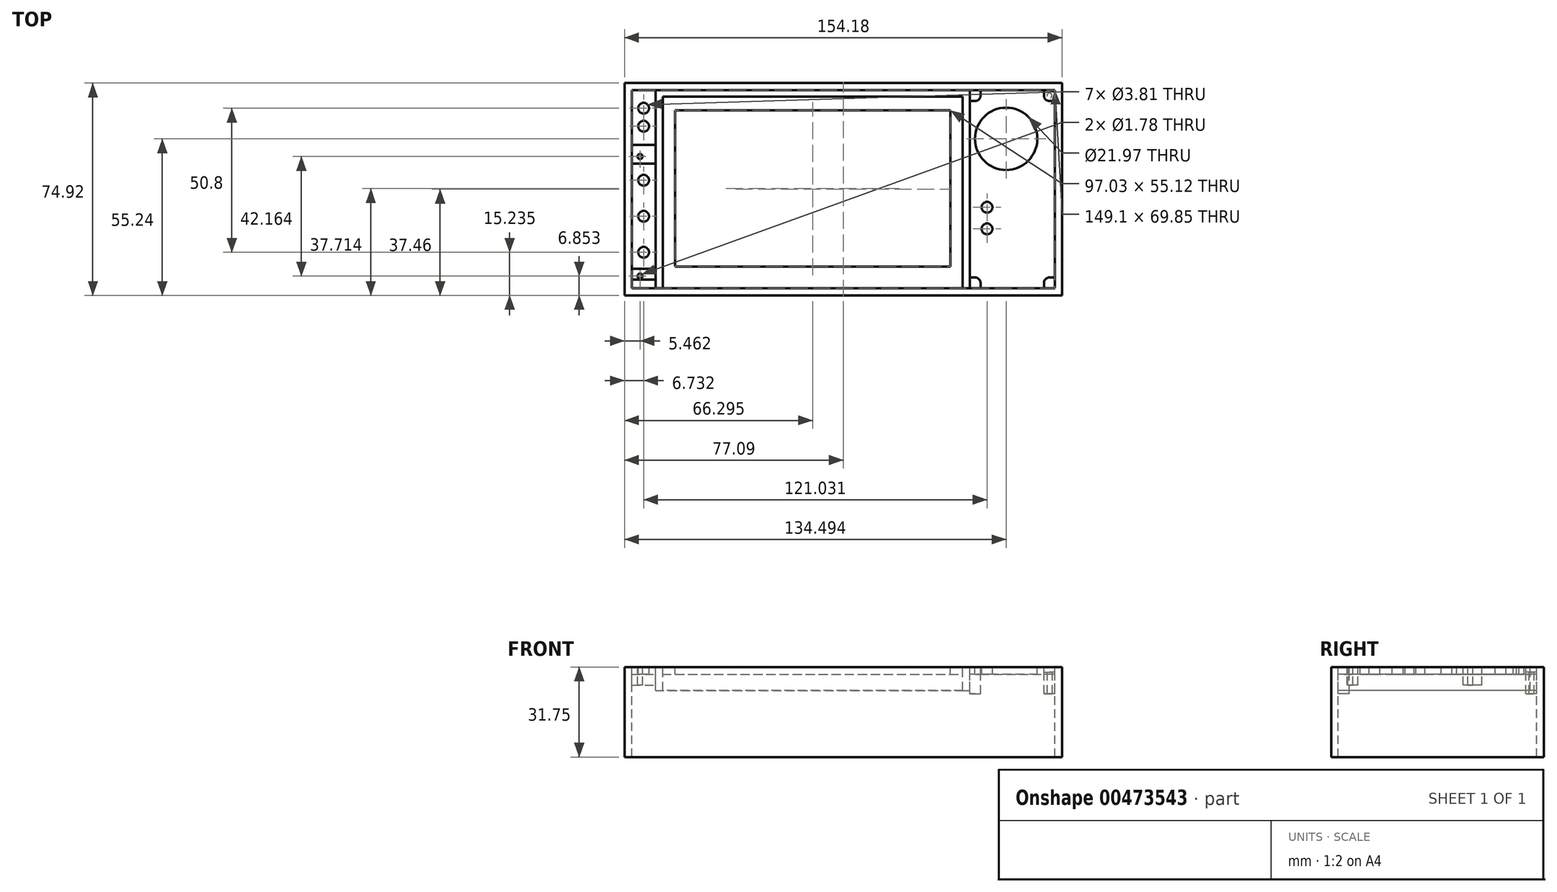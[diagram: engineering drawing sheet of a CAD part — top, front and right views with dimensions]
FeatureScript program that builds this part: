
annotation { "Feature Type Name" : "Feature", "Feature Type Description" : "" }
export const myFeature = defineFeature(function(context is Context, id is Id, definition is map)
    precondition{}
    {
        {
            var Q0;
            Q0=qCreatedBy(makeId("Top.planeOp"),FACE);
            var sketch = newSketch(context, id + "F0", { "sketchPlane" : qUnion([Q0])});
            skLineSegment(sketch, "E0.bottom", {"start": v(77.09, 37.47) * mm, "end": v(-77.09, 37.47) * mm});
            skLineSegment(sketch, "E0.top", {"start": v(77.09, -37.47) * mm, "end": v(-77.09, -37.47) * mm});
            skLineSegment(sketch, "E0.left", {"start": v(77.09, 37.47) * mm, "end": v(77.09, -37.47) * mm});
            skLineSegment(sketch, "E0.right", {"start": v(-77.09, 37.47) * mm, "end": v(-77.09, -37.47) * mm});
            skPoint(sketch, "E0.middle", {"position": v(0, 0) * mm});
            skLineSegment(sketch, "E1.bottom", {"start": v(-59.3, -27.3) * mm, "end": v(37.72, -27.3) * mm});
            skLineSegment(sketch, "E1.top", {"start": v(-59.3, 27.81) * mm, "end": v(37.72, 27.81) * mm});
            skLineSegment(sketch, "E1.left", {"start": v(-59.3, -27.3) * mm, "end": v(-59.3, 27.81) * mm});
            skLineSegment(sketch, "E1.right", {"start": v(37.72, -27.3) * mm, "end": v(37.72, 27.81) * mm});
            skCircle(sketch, "E2", {"center": v(57.4, 17.78) * mm, "radius": 9.53 * mm});
            skLineSegment(sketch, "E3", {"start": v(77.09, -1.9) * mm, "end": v(37.72, 37.47) * mm, "construction": true});
            skLineSegment(sketch, "E4", {"start": v(77.09, 37.47) * mm, "end": v(57.4, 17.78) * mm, "construction": true});
            skCircle(sketch, "E5", {"center": v(57.4, 17.78) * mm, "radius": 13.34 * mm, "construction": true});
            skCircle(sketch, "E6", {"center": v(47.97, 27.2) * mm, "radius": 0.89 * mm});
            skCircle(sketch, "E7", {"center": v(66.83, 8.35) * mm, "radius": 0.89 * mm});
            skCircle(sketch, "E8", {"center": v(57.4, 17.78) * mm, "radius": 10.99 * mm});
            skLineSegment(sketch, "E9.bottom", {"start": v(-74.55, 34.93) * mm, "end": v(74.55, 34.93) * mm});
            skLineSegment(sketch, "E9.top", {"start": v(-74.55, -34.92) * mm, "end": v(74.55, -34.93) * mm});
            skLineSegment(sketch, "E9.left", {"start": v(-63.63, 34.93) * mm, "end": v(-63.63, -34.93) * mm});
            skLineSegment(sketch, "E9.right", {"start": v(42.04, 34.93) * mm, "end": v(42.04, -34.93) * mm});
            skLineSegment(sketch, "E10", {"start": v(-66.17, 34.93) * mm, "end": v(-66.17, -34.93) * mm});
            skLineSegment(sketch, "E11", {"start": v(-74.55, 34.92) * mm, "end": v(-74.55, -34.92) * mm});
            skLineSegment(sketch, "E12", {"start": v(44.58, 34.93) * mm, "end": v(44.58, -34.93) * mm});
            skLineSegment(sketch, "E13", {"start": v(74.55, 34.93) * mm, "end": v(74.55, -34.93) * mm});
            skCircle(sketch, "E14", {"center": v(-70.36, 3.18) * mm, "radius": 1.9 * mm});
            skCircle(sketch, "E15", {"center": v(-70.36, -9.52) * mm, "radius": 1.9 * mm});
            skCircle(sketch, "E16", {"center": v(-70.36, -22.22) * mm, "radius": 1.9 * mm});
            skCircle(sketch, "E17", {"center": v(-70.36, 28.57) * mm, "radius": 1.9 * mm});
            skLineSegment(sketch, "E18", {"start": v(-70.36, 34.92) * mm, "end": v(-70.36, -34.93) * mm, "construction": true});
            skCircle(sketch, "E19", {"center": v(-70.36, 22.22) * mm, "radius": 1.9 * mm});
            skLineSegment(sketch, "E20", {"start": v(42.04, 32.64) * mm, "end": v(-63.63, 32.64) * mm});
            skLineSegment(sketch, "E21", {"start": v(44.58, -34.92) * mm, "end": v(74.55, -4.95) * mm, "construction": true});
            skLineSegment(sketch, "E22", {"start": v(74.55, -34.93) * mm, "end": v(44.58, -4.95) * mm, "construction": true});
            skCircle(sketch, "E23", {"center": v(72.64, 33.02) * mm, "radius": 0.89 * mm});
            skLineSegment(sketch, "E24", {"start": v(44.58, 34.93) * mm, "end": v(59.56, 19.94) * mm, "construction": true});
            skCircle(sketch, "E25", {"center": v(46.48, 33.02) * mm, "radius": 0.89 * mm});
            skCircle(sketch, "E26", {"center": v(46.48, -33.02) * mm, "radius": 0.89 * mm});
            skCircle(sketch, "E27", {"center": v(72.64, -33.02) * mm, "radius": 0.89 * mm});
            skArc(sketch, "E28", {"start": v(48.39, -33.02) * mm, "mid": v(47.83, -31.67) * mm, "end": v(46.48, -31.12) * mm});
            skArc(sketch, "E29", {"start": v(72.64, -31.12) * mm, "mid": v(71.3, -31.67) * mm, "end": v(70.74, -33.02) * mm});
            skArc(sketch, "E30", {"start": v(70.74, 33.02) * mm, "mid": v(71.3, 31.67) * mm, "end": v(72.64, 31.12) * mm});
            skArc(sketch, "E31", {"start": v(46.48, 31.12) * mm, "mid": v(47.83, 31.67) * mm, "end": v(48.39, 33.02) * mm});
            skLineSegment(sketch, "E32", {"start": v(46.48, 31.12) * mm, "end": v(44.58, 31.12) * mm});
            skLineSegment(sketch, "E33", {"start": v(48.39, 34.93) * mm, "end": v(48.39, 33.02) * mm});
            skLineSegment(sketch, "E34", {"start": v(70.74, 34.93) * mm, "end": v(70.74, 33.02) * mm});
            skLineSegment(sketch, "E35", {"start": v(74.55, 31.12) * mm, "end": v(72.64, 31.12) * mm});
            skLineSegment(sketch, "E36", {"start": v(74.55, -31.12) * mm, "end": v(72.64, -31.12) * mm});
            skLineSegment(sketch, "E37", {"start": v(70.74, -33.02) * mm, "end": v(70.74, -34.93) * mm});
            skLineSegment(sketch, "E38", {"start": v(48.39, -33.02) * mm, "end": v(48.39, -34.93) * mm});
            skLineSegment(sketch, "E39", {"start": v(46.48, -31.12) * mm, "end": v(44.58, -31.12) * mm});
            skCircle(sketch, "E40", {"center": v(50.67, -13.97) * mm, "radius": 1.9 * mm});
            skCircle(sketch, "E41", {"center": v(50.67, -6.35) * mm, "radius": 1.9 * mm});
            skLineSegment(sketch, "E42", {"start": v(-66.17, 9.02) * mm, "end": v(-74.55, 9.02) * mm});
            skLineSegment(sketch, "E43", {"start": v(-74.55, 15.62) * mm, "end": v(-66.17, 15.62) * mm});
            skLineSegment(sketch, "E44", {"start": v(-74.55, -28.07) * mm, "end": v(-63.63, -28.07) * mm});
            skLineSegment(sketch, "E45", {"start": v(-66.17, -31.88) * mm, "end": v(-74.55, -31.88) * mm});
            skCircle(sketch, "E46", {"center": v(-71.63, 11.56) * mm, "radius": 0.89 * mm});
            skCircle(sketch, "E47", {"center": v(-71.63, -30.6) * mm, "radius": 0.89 * mm});
            skLineSegment(sketch, "E48", {"start": v(-71.63, 11.56) * mm, "end": v(-70.36, -9.53) * mm, "construction": true});
            skLineSegment(sketch, "E49", {"start": v(-71.63, -30.6) * mm, "end": v(-70.36, -9.52) * mm, "construction": true});
            skSolve(sketch);
        }
        {
            var Q0;
            Q0=makeQuery(id+"F0.imprint","IMPRINT",FACE,{"disambiguationData":[TD([[makeQuery(id+"F0.imprint","IMPRINT",EDGE,{"derivedFrom":sQuery(id+"F0.wireOp",EDGE,"E0.bottom")}),1.0]])]});
            extrude(context, id + "F1", {"entities" : qUnion([Q0]), "oppositeDirection" : true, "depth" : 31.75 * mm, "offsetDistance" : 25.4 * mm});
        }
        {
            var Q0;
            {var subQ6=sQuery(id+"F0.wireOp",EDGE,"E10");Q0=makeQuery(id+"F0.imprint","IMPRINT",FACE,{"disambiguationData":[TD([[makeQuery(id+"F0.imprint","IMPRINT",EDGE,{"derivedFrom":subQ6}),1.0]])]});}
            var Q1;
            {var subQ0=sQuery(id+"F0.wireOp",EDGE,"E9.right");var subQ4=sQuery(id+"F0.wireOp",EDGE,"E9.bottom");var subQ5=makeQuery(id+"F0.imprint","INTERSECT",VERTEX,{"derivedFrom":[subQ4,subQ0]});Q1=makeQuery(id+"F0.imprint","IMPRINT",FACE,{"disambiguationData":[TD([[makeQuery(id+"F0.imprint","IMPRINT",EDGE,{"disambiguationData":[TD([[subQ5,-1.0]])],"derivedFrom":subQ4}),-1.0]])]});}
            var Q2;
            {var subQ5=sQuery(id+"F0.wireOp",EDGE,"E20");Q2=makeQuery(id+"F0.imprint","IMPRINT",FACE,{"disambiguationData":[TD([[makeQuery(id+"F0.imprint","IMPRINT",EDGE,{"derivedFrom":subQ5}),-1.0]])]});}
            var Q3;
            {var subQ4=sQuery(id+"F0.wireOp",EDGE,"E9.left");var subQ5=sQuery(id+"F0.wireOp",EDGE,"E9.top");var subQ6=makeQuery(id+"F0.imprint","INTERSECT",VERTEX,{"derivedFrom":[subQ5,subQ4]});Q3=makeQuery(id+"F0.imprint","IMPRINT",FACE,{"disambiguationData":[TD([[makeQuery(id+"F0.imprint","IMPRINT",EDGE,{"disambiguationData":[TD([[subQ6,1.0]])],"derivedFrom":subQ5}),1.0]])]});}
            extrude(context, id + "F2", {"entities" : qUnion([Q0, Q1, Q2, Q3]), "oppositeDirection" : true, "depth" : 8.25 * mm, "offsetDistance" : 25.4 * mm});
        }
        {
            var Q0;
            {var subQ1=sQuery(id+"F0.wireOp",EDGE,"E10");Q0=makeQuery(id+"F0.imprint","IMPRINT",FACE,{"disambiguationData":[TD([[makeQuery(id+"F0.imprint","IMPRINT",EDGE,{"derivedFrom":subQ1}),-1.0]])]});}
            var Q1;
            Q1=makeQuery(id+"F0.imprint","IMPRINT",FACE,{"disambiguationData":[TD([[makeQuery(id+"F0.imprint","IMPRINT",EDGE,{"derivedFrom":sQuery(id+"F0.wireOp",EDGE,"E6")}),-1.0]])]});
            var Q2;
            Q2=makeQuery(id+"F0.imprint","IMPRINT",FACE,{"disambiguationData":[TD([[makeQuery(id+"F0.imprint","IMPRINT",EDGE,{"derivedFrom":sQuery(id+"F0.wireOp",EDGE,"E1.bottom")}),-1.0]])]});
            var Q3;
            Q3=makeQuery(id+"F0.imprint","IMPRINT",FACE,{"disambiguationData":[TD([[makeQuery(id+"F0.imprint","IMPRINT",EDGE,{"derivedFrom":sQuery(id+"F0.wireOp",EDGE,"E6")}),1.0]])]});
            var Q4;
            Q4=makeQuery(id+"F0.imprint","IMPRINT",FACE,{"disambiguationData":[TD([[makeQuery(id+"F0.imprint","IMPRINT",EDGE,{"derivedFrom":sQuery(id+"F0.wireOp",EDGE,"E7")}),1.0]])]});
            var Q5;
            Q5=makeQuery(id+"F0.imprint","IMPRINT",FACE,{"disambiguationData":[TD([[makeQuery(id+"F0.imprint","IMPRINT",EDGE,{"derivedFrom":sQuery(id+"F0.wireOp",EDGE,"E14")}),-1.0]])]});
            var Q6;
            Q6=makeQuery(id+"F0.imprint","IMPRINT",FACE,{"disambiguationData":[TD([[makeQuery(id+"F0.imprint","IMPRINT",EDGE,{"derivedFrom":sQuery(id+"F0.wireOp",EDGE,"E17")}),-1.0]])]});
            var Q7;
            Q7=makeQuery(id+"F0.imprint","IMPRINT",FACE,{"disambiguationData":[TD([[makeQuery(id+"F0.imprint","IMPRINT",EDGE,{"derivedFrom":sQuery(id+"F0.wireOp",EDGE,"E47")}),1.0]])]});
            var Q8;
            Q8=makeQuery(id+"F0.imprint","IMPRINT",FACE,{"disambiguationData":[TD([[makeQuery(id+"F0.imprint","IMPRINT",EDGE,{"derivedFrom":sQuery(id+"F0.wireOp",EDGE,"E46")}),1.0]])]});
            extrude(context, id + "F3", {"entities" : qUnion([Q0, Q1, Q2, Q3, Q4, Q5, Q6, Q7, Q8]), "oppositeDirection" : true, "depth" : 2.54 * mm, "offsetDistance" : 25.4 * mm});
        }
        {
            var Q0;
            Q0=makeQuery(id+"F0.imprint","IMPRINT",FACE,{"disambiguationData":[TD([[makeQuery(id+"F0.imprint","IMPRINT",EDGE,{"derivedFrom":sQuery(id+"F0.wireOp",EDGE,"E25")}),-1.0]])]});
            var Q1;
            Q1=makeQuery(id+"F0.imprint","IMPRINT",FACE,{"disambiguationData":[TD([[makeQuery(id+"F0.imprint","IMPRINT",EDGE,{"derivedFrom":sQuery(id+"F0.wireOp",EDGE,"E23")}),-1.0]])]});
            var Q2;
            Q2=makeQuery(id+"F0.imprint","IMPRINT",FACE,{"disambiguationData":[TD([[makeQuery(id+"F0.imprint","IMPRINT",EDGE,{"derivedFrom":sQuery(id+"F0.wireOp",EDGE,"E27")}),-1.0]])]});
            var Q3;
            Q3=makeQuery(id+"F0.imprint","IMPRINT",FACE,{"disambiguationData":[TD([[makeQuery(id+"F0.imprint","IMPRINT",EDGE,{"derivedFrom":sQuery(id+"F0.wireOp",EDGE,"E27")}),1.0]])]});
            var Q4;
            Q4=makeQuery(id+"F0.imprint","IMPRINT",FACE,{"disambiguationData":[TD([[makeQuery(id+"F0.imprint","IMPRINT",EDGE,{"derivedFrom":sQuery(id+"F0.wireOp",EDGE,"E26")}),-1.0]])]});
            var Q5;
            Q5=makeQuery(id+"F0.imprint","IMPRINT",FACE,{"disambiguationData":[TD([[makeQuery(id+"F0.imprint","IMPRINT",EDGE,{"derivedFrom":sQuery(id+"F0.wireOp",EDGE,"E26")}),1.0]])]});
            var Q6;
            Q6=makeQuery(id+"F0.imprint","IMPRINT",FACE,{"disambiguationData":[TD([[makeQuery(id+"F0.imprint","IMPRINT",EDGE,{"derivedFrom":sQuery(id+"F0.wireOp",EDGE,"E25")}),1.0]])]});
            var Q7;
            Q7=makeQuery(id+"F0.imprint","IMPRINT",FACE,{"disambiguationData":[TD([[makeQuery(id+"F0.imprint","IMPRINT",EDGE,{"derivedFrom":sQuery(id+"F0.wireOp",EDGE,"E23")}),1.0]])]});
            extrude(context, id + "F4", {"entities" : qUnion([Q0, Q1, Q2, Q3, Q4, Q5, Q6, Q7]), "oppositeDirection" : true, "depth" : 9.4 * mm, "offsetDistance" : 25.4 * mm});
        }
        {
            var Q0;
            Q0=makeQuery(id+"F4.opExtrude","CAP_FACE",FACE,{"disambiguationData":[OSD([sQuery(id+"F0.wireOp",EDGE,"E9.bottom"),sQuery(id+"F0.wireOp",EDGE,"E13"),sQuery(id+"F0.wireOp",EDGE,"E30"),sQuery(id+"F0.wireOp",EDGE,"E34"),sQuery(id+"F0.wireOp",EDGE,"E35")])],"isStart":false});
            var sketch = newSketch(context, id + "F5", { "sketchPlane" : qUnion([Q0])});
            skCircle(sketch, "E50.0", {"center": v(46.48, 33.02) * mm, "radius": 0.89 * mm});
            skCircle(sketch, "E51.0", {"center": v(72.64, 33.02) * mm, "radius": 0.89 * mm});
            skCircle(sketch, "E52.0", {"center": v(46.48, -33.02) * mm, "radius": 0.89 * mm});
            skCircle(sketch, "E52.1", {"center": v(72.64, -33.02) * mm, "radius": 0.89 * mm});
            skSolve(sketch);
        }
        {
            var Q0;
            Q0=makeQuery(id+"F5.imprint","IMPRINT",FACE,{"disambiguationData":[TD([[makeQuery(id+"F5.imprint","IMPRINT",EDGE,{"derivedFrom":sQuery(id+"F5.wireOp",EDGE,"E52.0")}),-1.0]])]});
            var Q1;
            Q1=makeQuery(id+"F5.imprint","IMPRINT",FACE,{"disambiguationData":[TD([[makeQuery(id+"F5.imprint","IMPRINT",EDGE,{"derivedFrom":sQuery(id+"F5.wireOp",EDGE,"E52.1")}),-1.0]])]});
            var Q2;
            Q2=makeQuery(id+"F5.imprint","IMPRINT",FACE,{"disambiguationData":[TD([[makeQuery(id+"F5.imprint","IMPRINT",EDGE,{"derivedFrom":sQuery(id+"F5.wireOp",EDGE,"E50.0")}),-1.0]])]});
            var Q3;
            Q3=makeQuery(id+"F5.imprint","IMPRINT",FACE,{"disambiguationData":[TD([[makeQuery(id+"F5.imprint","IMPRINT",EDGE,{"derivedFrom":sQuery(id+"F5.wireOp",EDGE,"E51.0")}),-1.0]])]});
            extrude(context, id + "F6", {"entities" : qUnion([Q0, Q1, Q2, Q3]), "operationType" : NewBodyOperationType.REMOVE, "oppositeDirection" : true, "depth" : 7.62 * mm, "offsetDistance" : 25.4 * mm});
        }
        {
            var Q0;
            {var subQ0=sQuery(id+"F0.wireOp",EDGE,"E42");Q0=makeQuery(id+"F0.imprint","IMPRINT",FACE,{"disambiguationData":[TD([[makeQuery(id+"F0.imprint","IMPRINT",EDGE,{"derivedFrom":subQ0}),-1.0]])]});}
            var Q1;
            {var subQ0=sQuery(id+"F0.wireOp",EDGE,"E45");Q1=makeQuery(id+"F0.imprint","IMPRINT",FACE,{"disambiguationData":[TD([[makeQuery(id+"F0.imprint","IMPRINT",EDGE,{"derivedFrom":subQ0}),-1.0]])]});}
            extrude(context, id + "F7", {"entities" : qUnion([Q0, Q1]), "oppositeDirection" : true, "depth" : 6.35 * mm, "offsetDistance" : 25.4 * mm});
        }
    });
